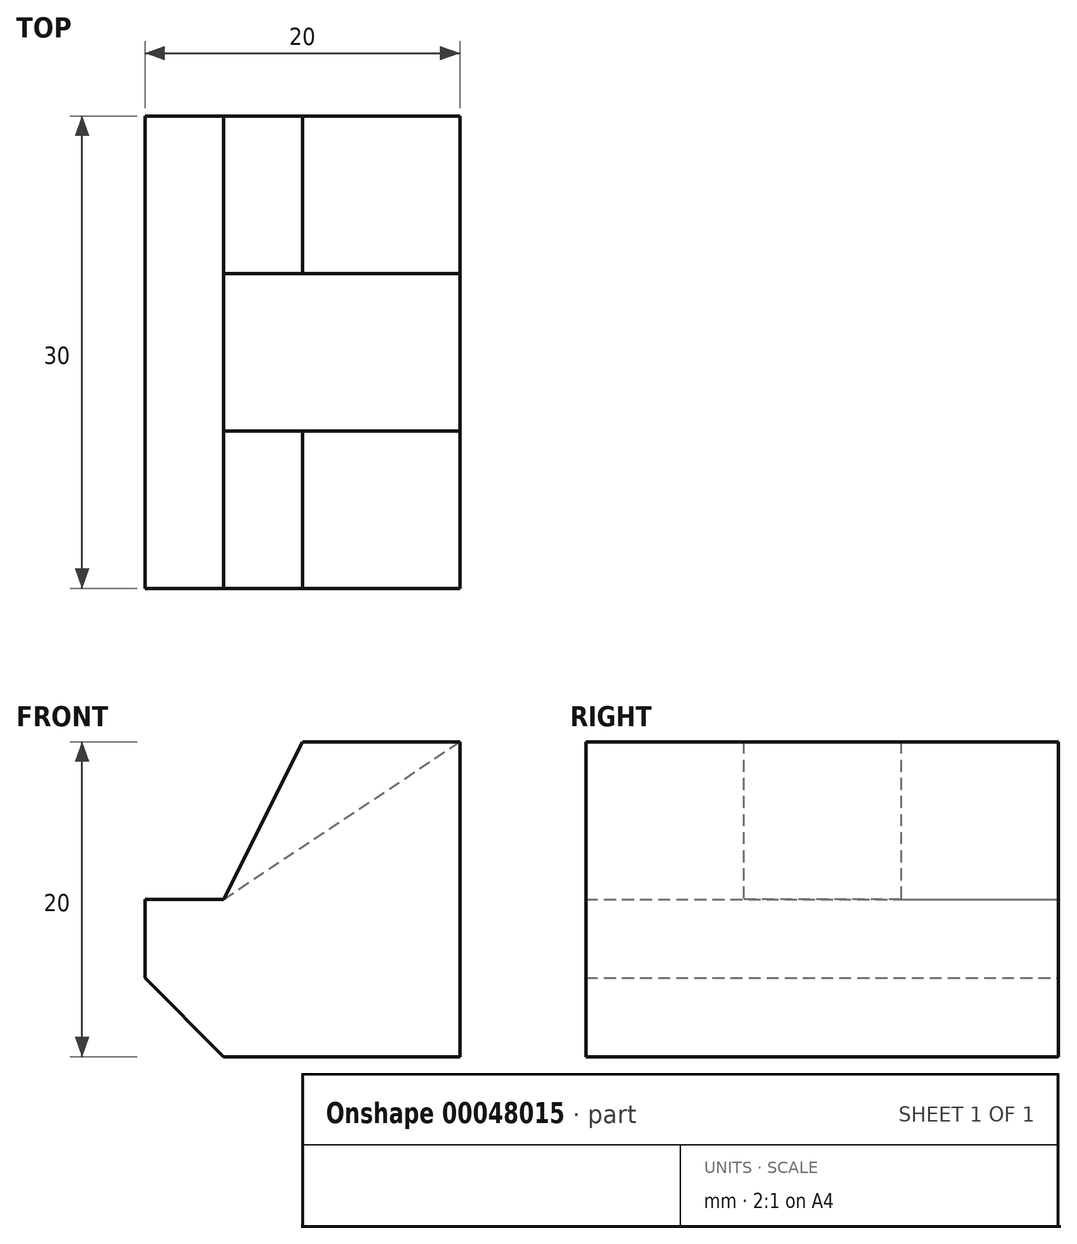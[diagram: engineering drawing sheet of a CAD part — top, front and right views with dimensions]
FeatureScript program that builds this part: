
annotation { "Feature Type Name" : "Feature", "Feature Type Description" : "" }
export const myFeature = defineFeature(function(context is Context, id is Id, definition is map)
    precondition{}
    {
        {
            var Q0;
            Q0=qCreatedBy(makeId("Front.planeOp"),FACE);
            var sketch = newSketch(context, id + "F0", { "sketchPlane" : qUnion([Q0])});
            skLineSegment(sketch, "E0", {"start": v(0, 0) * mm, "end": v(0, 20) * mm});
            skLineSegment(sketch, "E1", {"start": v(0, 20) * mm, "end": v(-10, 20) * mm});
            skLineSegment(sketch, "E2", {"start": v(-10, 20) * mm, "end": v(-15, 10) * mm});
            skLineSegment(sketch, "E3", {"start": v(-15, 10) * mm, "end": v(-20, 10) * mm});
            skLineSegment(sketch, "E4", {"start": v(-20, 10) * mm, "end": v(-20, 5) * mm});
            skLineSegment(sketch, "E5", {"start": v(-20, 5) * mm, "end": v(-15, 0) * mm});
            skLineSegment(sketch, "E6", {"start": v(-15, 0) * mm, "end": v(0, 0) * mm});
            skLineSegment(sketch, "E7", {"start": v(-15, 10) * mm, "end": v(0, 20) * mm});
            skSolve(sketch);
        }
        {
            var Q0;
            Q0 = qSketchRegion(id + "F0", true);
            extrude(context, id + "F1", {"entities" : qUnion([Q0]), "endBound" : BoundingType.SYMMETRIC, "depth" : 30 * mm});
        }
        {
            var Q0;
            Q0=makeQuery(id+"F0.imprint","IMPRINT",FACE,{"disambiguationData":[TD([[makeQuery(id+"F0.imprint","IMPRINT",EDGE,{"derivedFrom":sQuery(id+"F0.wireOp",EDGE,"E1")}),1.0]])]});
            extrude(context, id + "F2", {"entities" : qUnion([Q0]), "operationType" : NewBodyOperationType.REMOVE, "endBound" : BoundingType.SYMMETRIC, "oppositeDirection" : true, "depth" : 10 * mm});
        }
    });
